# Revit family: КШ-50-02
name_source: partatom
category: Арматура трубопроводов
units: mm (PartAtom-declared; Revit-internal decimal feet)

## family parameters
Всегда вертикально = Да
На основе рабочей плоскости = Нет
Общий = Нет
При загрузке вырезать с полостями = Нет
Размер круглого соединителя = Использовать диаметр
Тип детали = Клапан - Вставляется

## types (2) — shared parameters
ADSK_Единица измерения = шт.
ADSK_Завод-изготовитель = РУП "БЕЛГАЗТЕХНИКА"
ADSK_Класс герметичности по ГОСТ 9544-2005 = А
ADSK_Количество = 1
ADSK_Марка = КШ-50-02
ADSK_Направление потока = любое
ADSK_Тип крана по пропускной способности = с зауженным проходом
zero-valued in all types: Отметка по умолчанию

## per-type parameters (varying)
| type | ADSK_Масса_Текст | ADSK_Материал наименование | ADSK_Наименование | ADSK_Номинальное давление, МПа, не более |
| КШ Ду 50/36-1,2Ф | 8,7 кг | АК12 оч | Кран шаровой КШ Ду 50/36-1,2Ф ТУ РБ 05550283.055-98 | 1,2 |
| КШ Ду 50/36-0,6Ф | 20,0 кг | СЧ 20 | Кран шаровой КШ Ду 50/36-0,6Ф ТУ РБ 05550283.055-98 | 0,6 |
